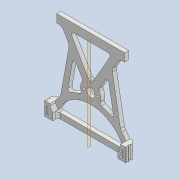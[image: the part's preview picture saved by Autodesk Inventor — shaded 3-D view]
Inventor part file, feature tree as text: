
AUTODESK INVENTOR PART (.ipt)
format: ipt  version: 2020 (Build 240168000, 168)  size: 450,560 bytes
history: native  units: mm
features: sketch x11, extrude x11, projected_geometry x10, mirror x4, fillet x4, reference x3, other x3, plane x2, chamfer x2, thicken_offset x1, pattern_circular x1
ambient origin geometry x8: Origin, YZ Plane, XZ Plane, XY Plane, X Axis, Y Axis, Z Axis, Center Point
bodies: Solid1 (feature_tree)
feature tree (52):
  sketch  "Sketch1"  dims[d0=30.0mm d1=20.0mm]
  plane  "Work Plane1"
  extrude  "Extrusion1"  Depth=20.0mm
  extrude  "Extrusion2"  Depth=4.0mm
  extrude  "Extrusion3"  Depth=10.0mm TaperAngle=0.0deg
  plane  "Work Plane2"
  mirror  "Mirror1"
  extrude  "Extrusion4"  Depth=5.0mm
  extrude  "Extrusion5"  Depth=10.0mm TaperAngle=0.0deg
  extrude  "Extrusion6"  Depth=2.0mm
  fillet  "Fillet1"  Radius=3.5mm
  extrude  "Extrusion7"  Depth=1.5mm
  extrude  "Extrusion8"  Depth=6.1mm
  mirror  "Mirror2"
  fillet  "Fillet2"  Radius=15.0mm
  fillet  "Fillet3"  Radius=3.0mm
  extrude  "Extrusion9"  Depth=4.0mm TaperAngle=0.0deg
  chamfer  "Chamfer1"  Distance=3.0mm
  fillet  "Fillet4"  Radius=1.0mm
  thicken_offset  "Thicken1"
  extrude  "Extrusion10"  Depth=6.0mm
  pattern_circular  "Circular Pattern1"  Count=5  [1 undecoded]
  mirror  "Mirror3"
  extrude  "Extrusion11"  Depth=20.0mm
  mirror  "Mirror4"
  chamfer  "Chamfer2"  Distance=5.0mm
  reference  "Reference1"
  sketch  "Sketch2"  dims[d2=8.0mm d3=4.0mm]
  projected_geometry  "Projected Loop1"
  sketch  "Sketch3"  dims[d4=10.0mm d5=10.0mm d6=0.0mm]
  projected_geometry  "Projected Loop2"
  sketch  "Sketch4"  dims[d7=2.0mm d8=5.0mm]
  projected_geometry  "Projected Loop3"
  projected_geometry  "Projected Loop4"
  sketch  "Sketch5"  dims[d9=30.0deg d10=10.0mm d11=0.0mm]
  projected_geometry  "Projected Loop5"
  sketch  "Sketch6"  dims[d12=2.2mm d13=2.0mm d14=3.5mm]
  projected_geometry  "Projected Loop6"
  sketch  "Sketch7"  dims[d15=1.5mm d16=1.5mm]
  projected_geometry  "Projected Loop7"
  sketch  "Sketch8"  dims[d17=10.0mm d18=0.0mm d19=6.1mm d20=15.0mm d21=3.0mm d22=0.0mm]
  projected_geometry  "Projected Loop8"
  sketch  "Sketch9"  dims[d23=2.5mm d24=4.0mm d25=0.0mm]
  reference  "Reference2"
  reference  "Reference3"
  projected_geometry  "Projected Loop9"
  sketch  "Sketch10"  dims[d26=4.0mm d27=3.0mm d28=0.0mm d29=1.0mm]
  sketch  "Sketch11"  dims[d30=35.0mm d31=6.0mm d32=50.0mm d33=20.0mm d34=5.0mm d35=20.0mm d36=5.0mm d37=3.0mm d38=0.0mm d39=4.0mm d40=3.0mm d41=0.0mm d42=1.5mm d43=4.0mm d44=1.5mm d45=1.5mm d46=3.0mm d47=0.0mm d48=2.0mm d49=2.0mm d50=45.0deg d51=2.0mm d52=4.0mm d53=4.0mm d54=5.0mm d55=1.8mm d56=3.0mm d57=0.0mm d58=40.0mm d59=360.0deg d61=1.8mm d62=3.0mm d63=2.5mm d64=0.5mm d65=9.0mm d66=0.0mm d67=0.3mm d68=2.0mm d69=45.0deg]
  projected_geometry  "Projected Loop10"
  parser-record x1  (decoder bookkeeping rows leaked as tree rows — omitted from the tree; the rows remain in map.json)
  other  "driver_unit_1.iam"
  other  "driver_wheel_1:1"
note: 1 required parameter value undecoded (feature->parameter linkage not recoverable at this tier; creation-order binding heuristic only, values carry confidence <= 0.55)
note: 1 file-system path scrubbed to <path> (originals preserved in map.json)
